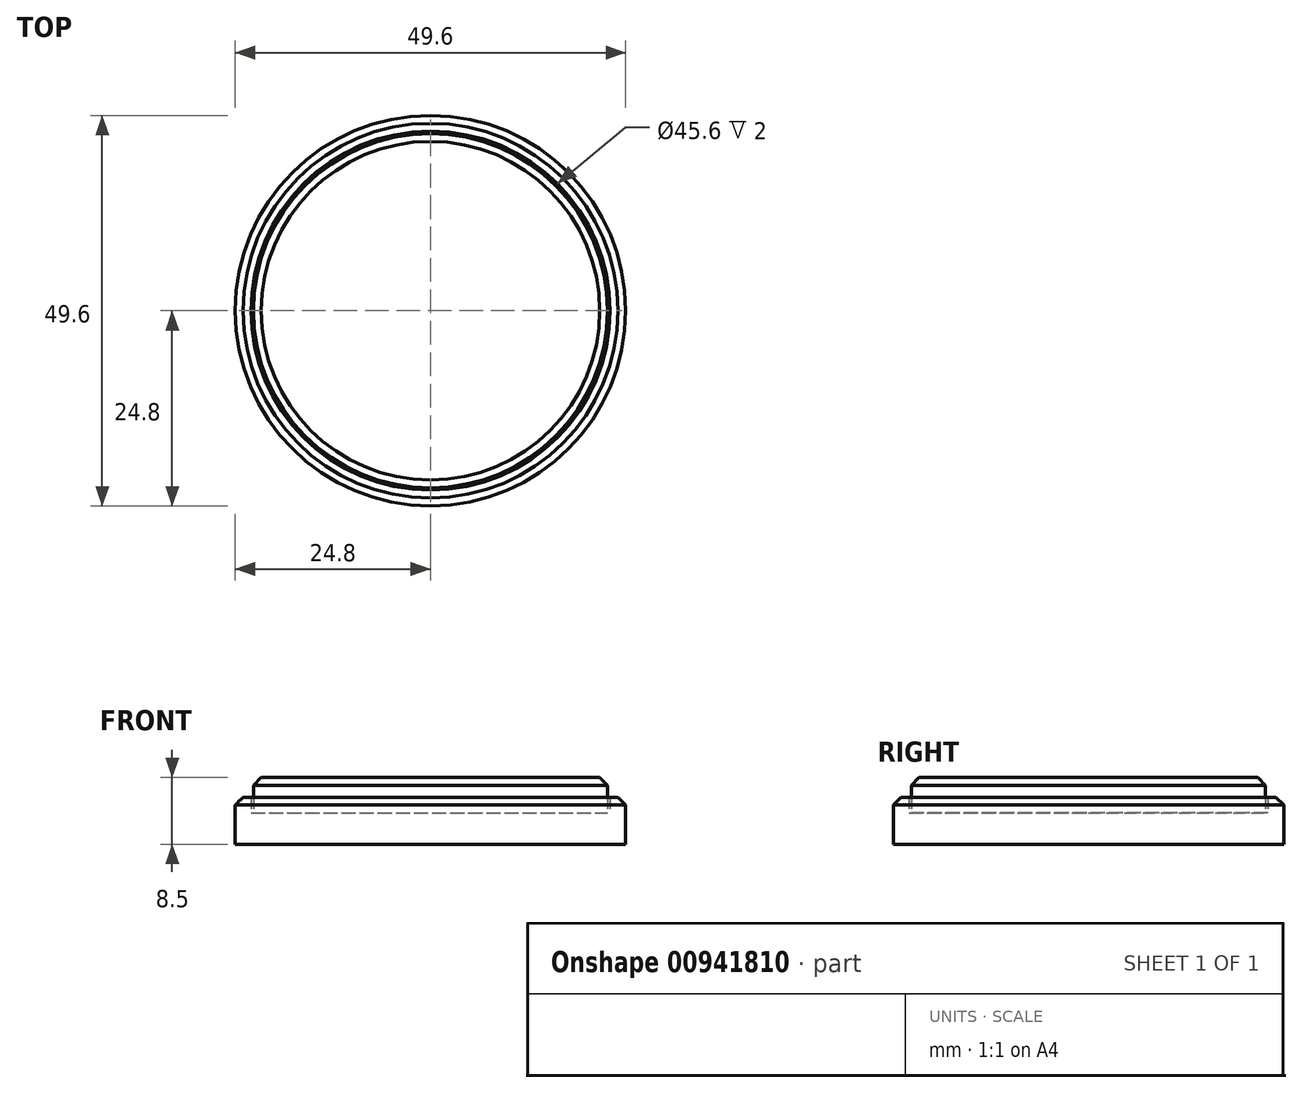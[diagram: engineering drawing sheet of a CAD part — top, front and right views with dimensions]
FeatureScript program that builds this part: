
annotation { "Feature Type Name" : "Feature", "Feature Type Description" : "" }
export const myFeature = defineFeature(function(context is Context, id is Id, definition is map)
    precondition{}
    {
        {
            var Q0;
            Q0=qCreatedBy(makeId("Front.planeOp"),FACE);
            var sketch = newSketch(context, id + "F0", { "sketchPlane" : qUnion([Q0])});
            skLineSegment(sketch, "E0.bottom", {"start": v(0, 0) * mm, "end": v(-22.5, 0) * mm});
            skLineSegment(sketch, "E0.top", {"start": v(0, 2.5) * mm, "end": v(-20, 2.5) * mm});
            skLineSegment(sketch, "E0.left", {"start": v(0, 0) * mm, "end": v(0, 2.5) * mm});
            skLineSegment(sketch, "E0.right", {"start": v(-22.5, 0) * mm, "end": v(-22.5, 2.5) * mm});
            skLineSegment(sketch, "E1.top", {"start": v(-22.5, 4.5) * mm, "end": v(-20, 4.5) * mm});
            skLineSegment(sketch, "E1.left", {"start": v(-22.5, 2.5) * mm, "end": v(-22.5, 4.5) * mm});
            skLineSegment(sketch, "E1.right", {"start": v(-20, 2.5) * mm, "end": v(-20, 4.5) * mm});
            skPoint(sketch, "E2.middle", {"position": v(-22.5, 2.5) * mm});
            skPoint(sketch, "E3.middle", {"position": v(-22.5, 1.25) * mm});
            skLineSegment(sketch, "E4.bottom", {"start": v(-20, 4.5) * mm, "end": v(0, 4.5) * mm});
            skLineSegment(sketch, "E4.top", {"start": v(-20, 2.5) * mm, "end": v(0, 2.5) * mm});
            skLineSegment(sketch, "E4.left", {"start": v(-20, 4.5) * mm, "end": v(-20, 2.5) * mm});
            skLineSegment(sketch, "E4.right", {"start": v(0, 4.5) * mm, "end": v(0, 2.5) * mm});
            skSolve(sketch);
        }
        {
            var Q0;
            Q0=makeQuery(id+"F0.imprint","IMPRINT",FACE,{"disambiguationData":[TD([[makeQuery(id+"F0.imprint","IMPRINT",EDGE,{"derivedFrom":sQuery(id+"F0.wireOp",EDGE,"E0.bottom")}),-1.0]])]});
            var Q1;
            Q1=makeQuery(id+"F0.imprint","IMPRINT",FACE,{"disambiguationData":[TD([[makeQuery(id+"F0.imprint","IMPRINT",EDGE,{"derivedFrom":sQuery(id+"F0.wireOp",EDGE,"E4.bottom")}),-1.0]])]});
            var Q2;
            Q2=sQuery(id+"F0.wireOp",EDGE,"E0.left");
            revolve(context, id + "F1", {"surfaceOperationType" : NewSurfaceOperationType.NEW, "entities" : qUnion([Q0, Q1]), "axis" : qUnion([Q2]), "revolveType" : RevolveType.FULL});
        }
        {
            var Q0;
            Q0=makeQuery(id+"F1.opRevolve","SWEPT_EDGE",EDGE,{"disambiguationData":[OSD([sQuery(id+"F0.wireOp",EDGE,"E1.top"),sQuery(id+"F0.wireOp",EDGE,"E1.left")])]});
            var Q1;
            Q1=makeQuery(id+"F1.opRevolve","SWEPT_FACE",FACE,{"disambiguationData":[OSD([sQuery(id+"F0.wireOp",EDGE,"E0.top")])]});
            chamfer(context, id + "F2", {"entities" : qUnion([Q0, Q1]), "width" : 1 * mm, "tangentPropagation" : true});
        }
        {
            var Q0;
            Q0=makeQuery(id+"F1.opRevolve","SWEPT_FACE",FACE,{"disambiguationData":[OSD([sQuery(id+"F0.wireOp",EDGE,"E0.bottom")])]});
            var sketch = newSketch(context, id + "F3", { "sketchPlane" : qUnion([Q0])});
            skCircle(sketch, "E5.0", {"center": v(0, 0) * mm, "radius": 22.8 * mm});
            skCircle(sketch, "E6.0", {"center": v(0, 0) * mm, "radius": 24.8 * mm});
            skSolve(sketch);
        }
        {
            var Q0;
            Q0 = qSketchRegion(id + "F3", true);
            var Q1;
            Q1=makeQuery(id+"F3.imprint","IMPRINT",FACE,{"disambiguationData":[TD([[makeQuery(id+"F3.imprint","IMPRINT",EDGE,{"derivedFrom":makeQuery(id+"F1.opRevolve","SWEPT_EDGE",EDGE,{"disambiguationData":[OSD([sQuery(id+"F0.wireOp",EDGE,"E0.bottom"),sQuery(id+"F0.wireOp",EDGE,"E0.right")])]})}),1.0]])]});
            var Q2;
            Q2=makeQuery(id+"F3.imprint","IMPRINT",FACE,{"disambiguationData":[TD([[makeQuery(id+"F3.imprint","IMPRINT",EDGE,{"derivedFrom":sQuery(id+"F3.wireOp",EDGE,"E5.0")}),1.0]])]});
            extrude(context, id + "F4", {"entities" : qUnion([Q0, Q1, Q2]), "depth" : 4 * mm, "offsetDistance" : 25 * mm});
        }
        {
            var Q0;
            Q0=makeQuery(id+"F3.imprint","IMPRINT",FACE,{"disambiguationData":[TD([[makeQuery(id+"F3.imprint","IMPRINT",EDGE,{"derivedFrom":sQuery(id+"F3.wireOp",EDGE,"E5.0")}),-1.0]])]});
            extrude(context, id + "F5", {"entities" : qUnion([Q0]), "operationType" : NewBodyOperationType.ADD, "oppositeDirection" : true, "depth" : 2 * mm, "offsetDistance" : 25 * mm});
        }
        {
            var Q0;
            Q0=makeQuery(id+"F5.opExtrude","CAP_EDGE",EDGE,{"disambiguationData":[OSD([sQuery(id+"F3.wireOp",EDGE,"E6.0")])],"isStart":false});
            chamfer(context, id + "F6", {"entities" : qUnion([Q0]), "width" : 1 * mm, "tangentPropagation" : true});
        }
    });
